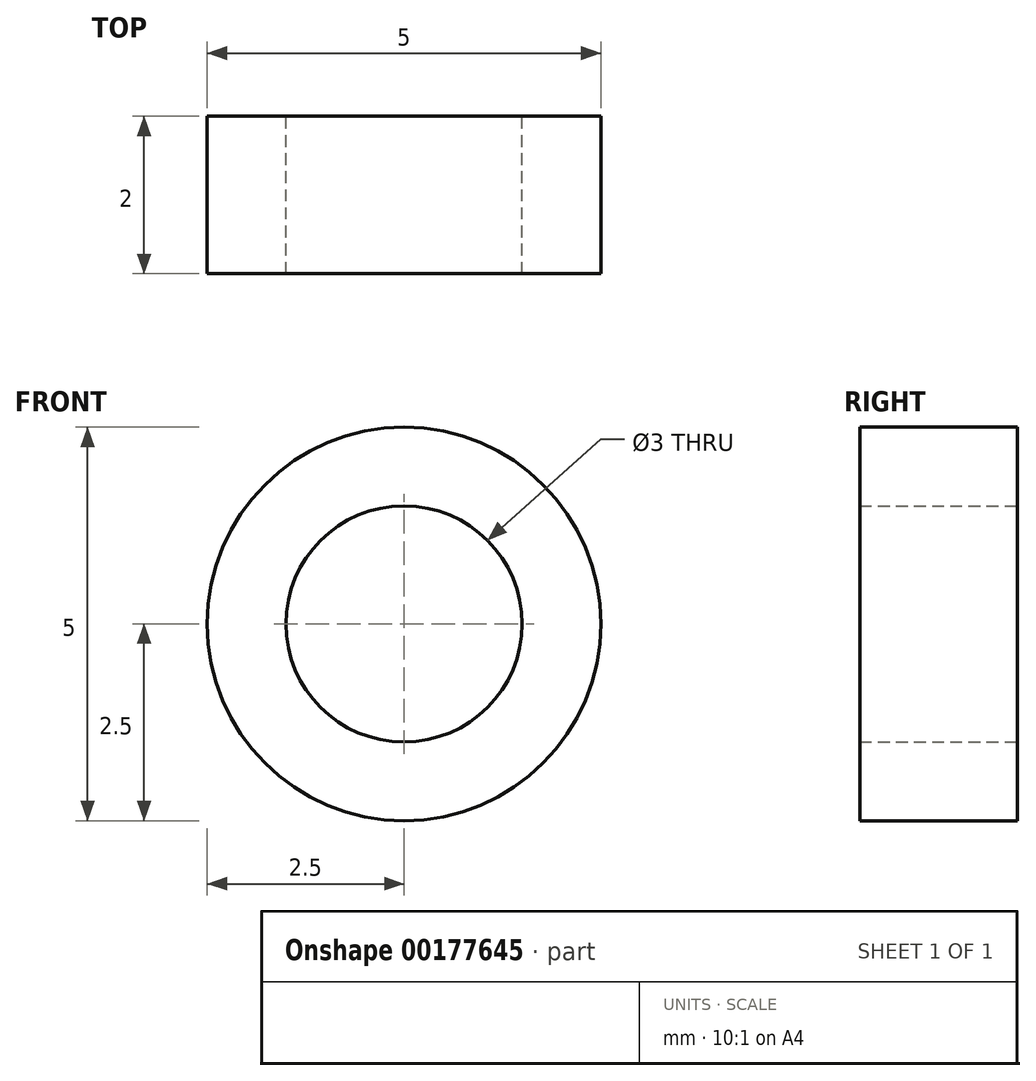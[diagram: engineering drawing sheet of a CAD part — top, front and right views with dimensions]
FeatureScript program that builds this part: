
annotation { "Feature Type Name" : "Feature", "Feature Type Description" : "" }
export const myFeature = defineFeature(function(context is Context, id is Id, definition is map)
    precondition{}
    {
        {
            var Q0;
            Q0=qCreatedBy(makeId("Front.planeOp"),FACE);
            var sketch = newSketch(context, id + "F0", { "sketchPlane" : qUnion([Q0])});
            skCircle(sketch, "E0", {"center": v(0, 0) * mm, "radius": 2.5 * mm});
            skCircle(sketch, "E1", {"center": v(0, 0) * mm, "radius": 1.5 * mm});
            skSolve(sketch);
        }
        {
            var Q0;
            Q0=qSketchRegion(id+"F0",true);
            extrude(context, id + "F1", {"entities" : qUnion([Q0]), "depth" : 2 * mm});
        }
    });
